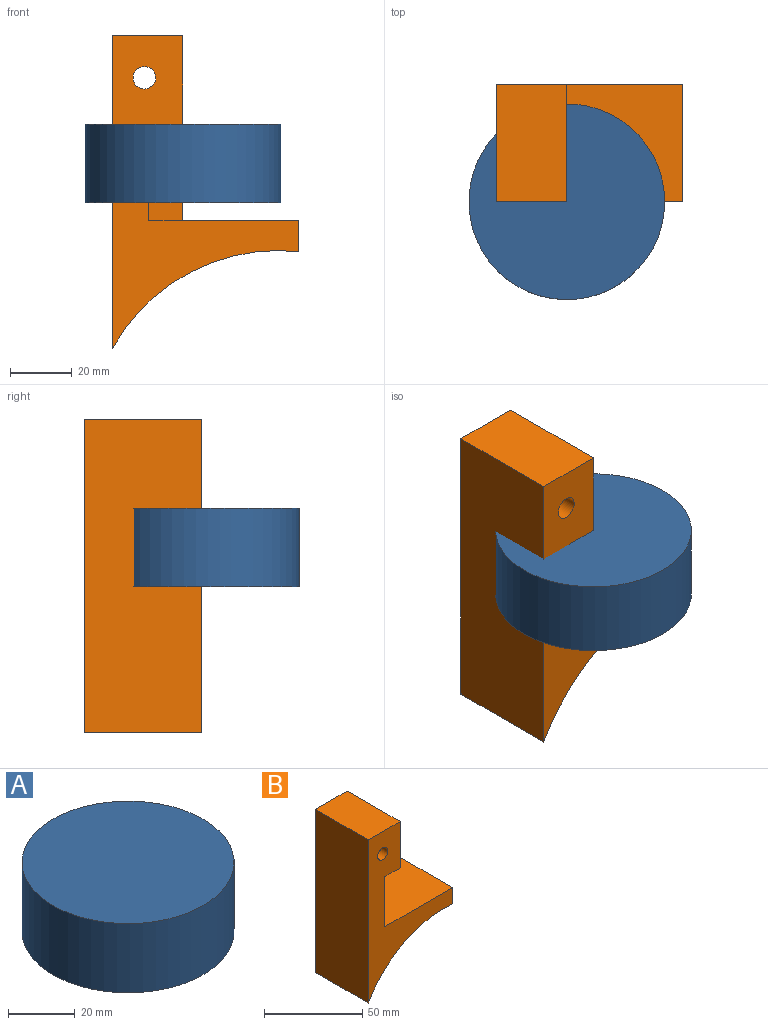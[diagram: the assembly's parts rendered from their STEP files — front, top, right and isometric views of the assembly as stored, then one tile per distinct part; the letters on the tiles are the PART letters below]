
ASSEMBLY  parts=2 mates=1
PART A: 3 faces, bbox 63.6x63.6x25.4 mm
  f0: cylinder r=31.79mm len=63.58mm, axis (0,0,-1), area 5073.6mm2, adj f1,f2
  f1: plane 63.58x63.58mm, normal (0,0,1), area 3175mm2, adj f0
  f2: plane 63.58x63.58mm, normal (0,0,-1), area 3175mm2, adj f0
PART B: 12 faces, bbox 60.6x38.1x101.6 mm
  f0: plane 48.72x38.1mm, normal (0,0,1), area 1671.7mm2, adj f1,f3,f7,f9,f10,f11
  f1: plane 31.19x21.34mm, normal (1,0,0), area 665.4mm2, adj f0,f2,f9,f11
  f2: plane 21.34x11.01mm, normal (0,0,-1), area 234.8mm2, adj f1,f3,f9,f11
  f3: plane 60x38.1mm, normal (1,0,0), area 1620.6mm2, adj f0,f2,f4,f9,f10,f11
  f4: plane 38.1x22.86mm, normal (0,0,1), area 871mm2, adj f3,f5,f9,f10
  f5: plane 101.6x38.1mm, normal (-1,0,0), area 3871mm2, adj f4,f6,f9,f10
  f6: cylinder r=61.74mm len=60.57mm, axis (0,1,0), area 2755mm2, adj f5,f7,f9,f10
  f7: plane 38.1x10.16mm, normal (1,0,0), area 387.1mm2, adj f0,f6,f9,f10
  f8: cylinder r=3.67mm len=38.1mm, axis (0,1,0), area 878.3mm2, adj f9,f10
  f9: plane 101.6x60.57mm, normal (0,-1,0), area 2077.2mm2, adj f0,f1,f2,f3,f4,f5,f6,f7
  f10: plane 101.6x60.57mm, normal (0,1,0), area 2420.5mm2, adj f0,f3,f4,f5,f6,f7,f8
  f11: plane 31.19x11.01mm, normal (0,-1,0), area 343.2mm2, adj f0,f1,f2,f3
PLACE A t=(26.38,-20.09,19.26)mm
PLACE B t=(-4.08,5.77,18.49)mm
MATE fastened A.f0 <-> B.f2  axis (0,0,1) through (-19.3,-32.33,44.66)mm
